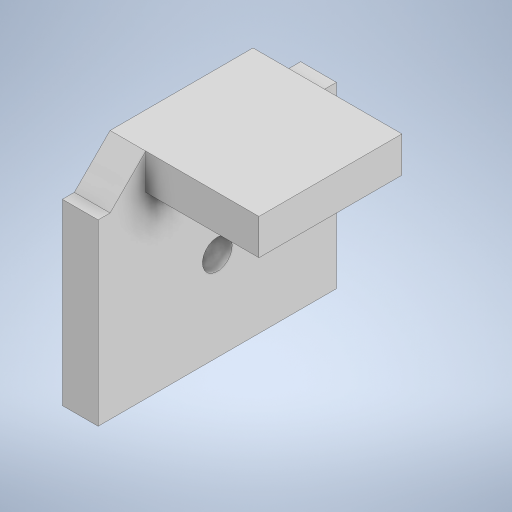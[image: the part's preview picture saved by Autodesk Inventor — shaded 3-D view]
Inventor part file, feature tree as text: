
AUTODESK INVENTOR PART (.ipt)
format: ipt  version: 2024 (Build 280153000, 153)  size: 230,912 bytes
history: native  units: mm
features: extrude x2, other x1, sketch x1, chamfer x1
ambient origin geometry x8: Origin, YZ Plane, XZ Plane, XY Plane, X Axis, Y Axis, Z Axis, Center Point
bodies: Body1 (feature_tree)
feature tree (5):
  other  "솔리드1"
  sketch  "스케치1"
  extrude  "돌출1"  Depth=15.0mm
  extrude  "돌출2"  Depth=20.0mm
  chamfer  "모따기1"  Distance=2.5mm
